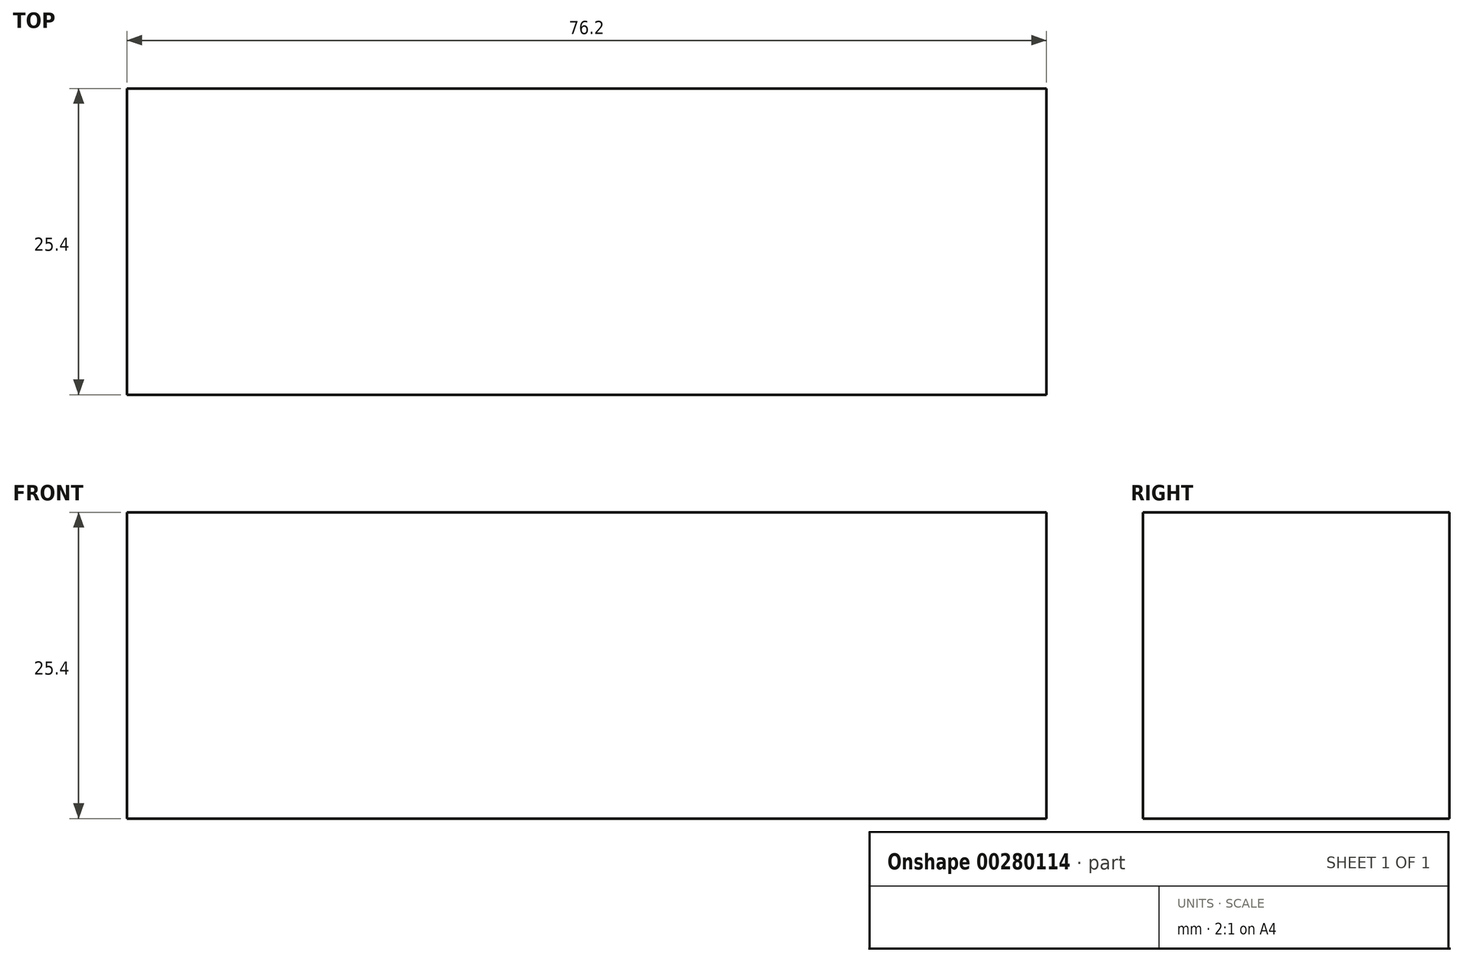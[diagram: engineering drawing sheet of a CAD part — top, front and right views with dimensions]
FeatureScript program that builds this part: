
annotation { "Feature Type Name" : "Feature", "Feature Type Description" : "" }
export const myFeature = defineFeature(function(context is Context, id is Id, definition is map)
    precondition{}
    {
        {
            var Q0;
            Q0=qCreatedBy(makeId("Front.planeOp"),FACE);
            var sketch = newSketch(context, id + "F0", { "sketchPlane" : qUnion([Q0])});
            skLineSegment(sketch, "E0", {"start": v(0, 0) * mm, "end": v(-76.2, 0) * mm});
            skLineSegment(sketch, "E1", {"start": v(-76.2, 0) * mm, "end": v(-76.2, 25.4) * mm});
            skLineSegment(sketch, "E2", {"start": v(-76.2, 25.4) * mm, "end": v(0, 25.4) * mm});
            skLineSegment(sketch, "E3", {"start": v(0, 25.4) * mm, "end": v(0, 0) * mm});
            skSolve(sketch);
        }
        {
            var Q0;
            Q0=makeQuery(id+"F0.imprint","IMPRINT",FACE,{"disambiguationData":[TD([[makeQuery(id+"F0.imprint","IMPRINT",EDGE,{"derivedFrom":sQuery(id+"F0.wireOp",EDGE,"E0")}),-1.0]])]});
            extrude(context, id + "F1", {"entities" : qUnion([Q0]), "depth" : 25.4 * mm});
        }
    });
